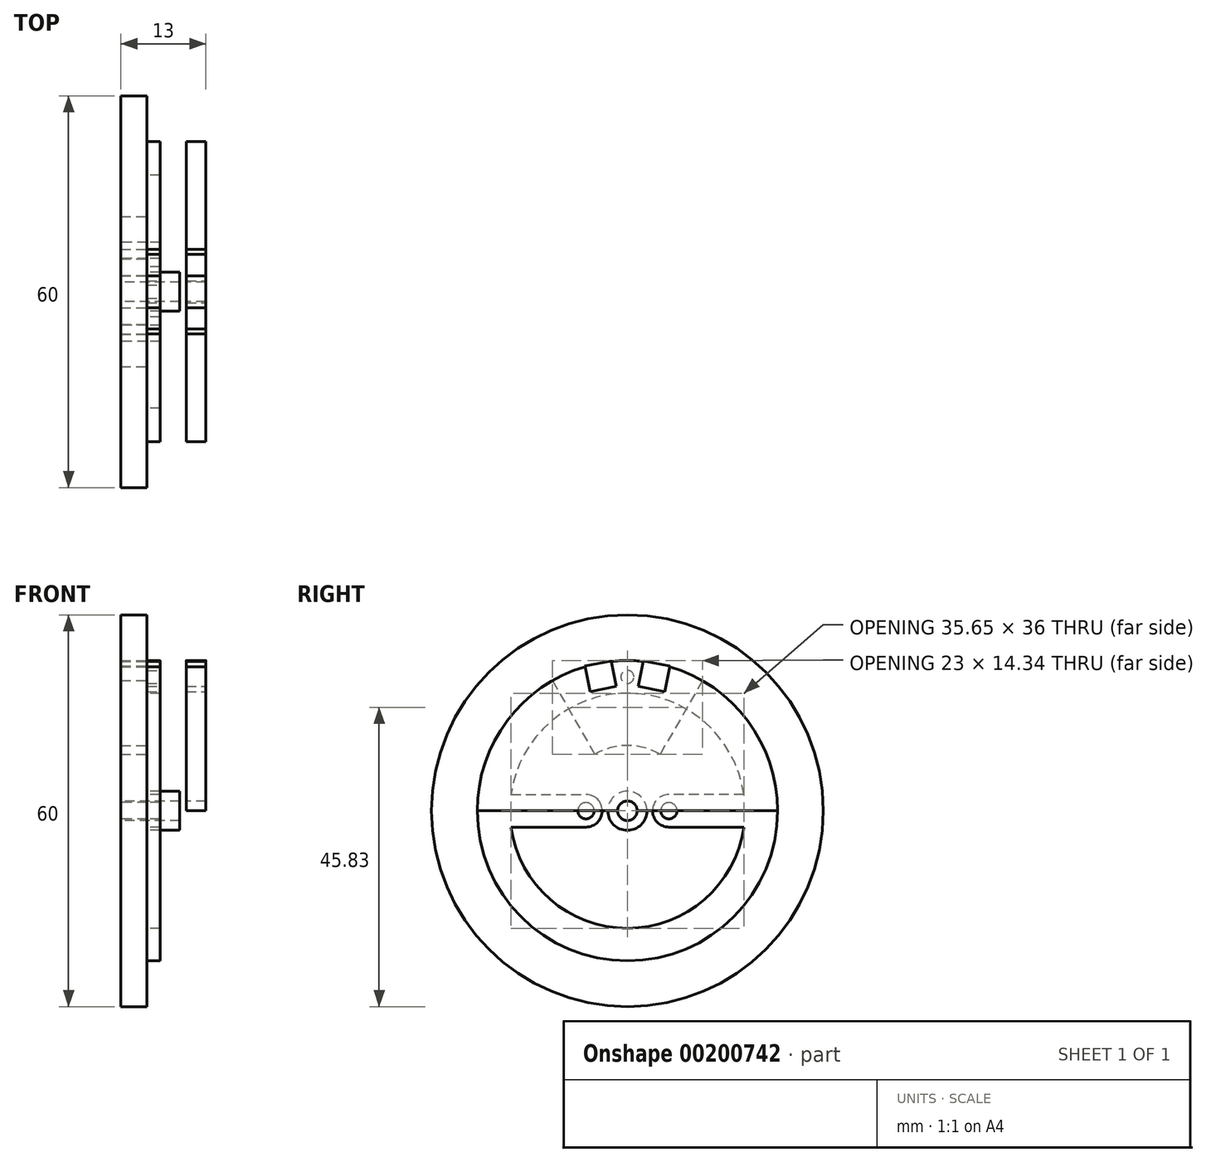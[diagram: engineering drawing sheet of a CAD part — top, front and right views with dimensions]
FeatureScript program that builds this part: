
annotation { "Feature Type Name" : "Feature", "Feature Type Description" : "" }
export const myFeature = defineFeature(function(context is Context, id is Id, definition is map)
    precondition{}
    {
        {
            var Q0;
            Q0=qCreatedBy(makeId("Right.planeOp"),FACE);
            var sketch = newSketch(context, id + "F0", { "sketchPlane" : qUnion([Q0])});
            skCircle(sketch, "E0", {"center": v(0, 0) * mm, "radius": 30 * mm});
            skSolve(sketch);
        }
        {
            var Q0;
            Q0 = qSketchRegion(id + "F0", true);
            extrude(context, id + "F1", {"entities" : qUnion([Q0]), "depth" : 4 * mm, "offsetDistance" : 25 * mm});
        }
        {
            var Q0;
            Q0=makeQuery(id+"F1.opExtrude","CAP_FACE",FACE,{"disambiguationData":[OSD([sQuery(id+"F0.wireOp",EDGE,"E0")])],"isStart":false});
            var sketch = newSketch(context, id + "F2", { "sketchPlane" : qUnion([Q0])});
            skCircle(sketch, "E1", {"center": v(0, 0) * mm, "radius": 3 * mm});
            skSolve(sketch);
        }
        {
            var Q0;
            Q0 = qSketchRegion(id + "F2", true);
            extrude(context, id + "F3", {"entities" : qUnion([Q0]), "operationType" : NewBodyOperationType.ADD, "depth" : 5 * mm, "offsetDistance" : 25 * mm});
        }
        {
            var Q0;
            Q0=makeQuery(id+"F1.opExtrude","CAP_FACE",FACE,{"disambiguationData":[OSD([sQuery(id+"F0.wireOp",EDGE,"E0")])],"isStart":true});
            var sketch = newSketch(context, id + "F4", { "sketchPlane" : qUnion([Q0])});
            skCircle(sketch, "E2", {"center": v(-6.35, 0) * mm, "radius": 1.25 * mm});
            skCircle(sketch, "E3.MirrorC", {"center": v(6.35, 0) * mm, "radius": 1.25 * mm});
            skCircle(sketch, "E4", {"center": v(0, 0) * mm, "radius": 1.5 * mm});
            skSolve(sketch);
        }
        {
            var Q0;
            Q0 = qSketchRegion(id + "F4", true);
            extrude(context, id + "F5", {"entities" : qUnion([Q0]), "operationType" : NewBodyOperationType.REMOVE, "endBound" : BoundingType.THROUGH_ALL, "oppositeDirection" : true, "depth" : 25 * mm, "offsetDistance" : 25 * mm});
        }
        {
            var Q0;
            Q0=makeQuery(id+"F1.opExtrude","CAP_FACE",FACE,{"disambiguationData":[OSD([sQuery(id+"F0.wireOp",EDGE,"E0")])],"isStart":false});
            var sketch = newSketch(context, id + "F6", { "sketchPlane" : qUnion([Q0])});
            skArc(sketch, "E5", {"start": v(11.5, 19.92) * mm, "mid": v(0, 23) * mm, "end": v(-11.5, 19.92) * mm});
            skArc(sketch, "E6", {"start": v(5, 8.66) * mm, "mid": v(0, 10) * mm, "end": v(-5, 8.66) * mm});
            skLineSegment(sketch, "E7", {"start": v(-11.5, 19.92) * mm, "end": v(-5, 8.66) * mm});
            skLineSegment(sketch, "E8", {"start": v(11.5, 19.92) * mm, "end": v(5, 8.66) * mm});
            skSolve(sketch);
        }
        {
            var Q0;
            Q0 = qSketchRegion(id + "F6", true);
            extrude(context, id + "F7", {"entities" : qUnion([Q0]), "operationType" : NewBodyOperationType.REMOVE, "endBound" : BoundingType.THROUGH_ALL, "oppositeDirection" : true, "depth" : 25 * mm, "offsetDistance" : 25 * mm});
        }
        {
            var Q0;
            Q0=makeQuery(id+"F1.opExtrude","CAP_FACE",FACE,{"disambiguationData":[OSD([sQuery(id+"F0.wireOp",EDGE,"E0")])],"isStart":false});
            var sketch = newSketch(context, id + "F8", { "sketchPlane" : qUnion([Q0])});
            skCircle(sketch, "E9", {"center": v(0, 0) * mm, "radius": 23 * mm});
            skArc(sketch, "E10", {"start": v(-17.83, -2.5) * mm, "mid": v(0, -18) * mm, "end": v(17.83, -2.5) * mm});
            skLineSegment(sketch, "E11.bottom", {"start": v(-17.83, 2.5) * mm, "end": v(-6.35, 2.5) * mm});
            skLineSegment(sketch, "E11.top", {"start": v(-17.83, -2.5) * mm, "end": v(-6.35, -2.5) * mm});
            skArc(sketch, "E12", {"start": v(-6.35, -2.5) * mm, "mid": v(-3.85, 0) * mm, "end": v(-6.35, 2.5) * mm});
            skLineSegment(sketch, "E13.MirrorCS", {"start": v(17.83, 2.5) * mm, "end": v(6.35, 2.5) * mm});
            skArc(sketch, "E14.MirrorCS", {"start": v(6.35, -2.5) * mm, "mid": v(3.85, 0) * mm, "end": v(6.35, 2.5) * mm});
            skLineSegment(sketch, "E15.MirrorCS", {"start": v(17.83, -2.5) * mm, "end": v(6.35, -2.5) * mm});
            skPoint(sketch, "E11.left.end.orphan", {"position": v(-22.86, -2.5) * mm});
            skPoint(sketch, "E11.left.start.orphan", {"position": v(-22.86, 2.5) * mm});
            skPoint(sketch, "E16.orphan", {"position": v(22.86, 2.5) * mm});
            skArc(sketch, "E17.trimOffspring", {"start": v(17.83, 2.5) * mm, "mid": v(0, 18) * mm, "end": v(-17.83, 2.5) * mm});
            skPoint(sketch, "E18.orphan", {"position": v(22.86, -2.5) * mm});
            skCircle(sketch, "E19.0", {"center": v(-6.35, 0) * mm, "radius": 1.25 * mm});
            skCircle(sketch, "E20.0", {"center": v(6.35, 0) * mm, "radius": 1.25 * mm});
            skSolve(sketch);
        }
        {
            var Q0;
            Q0 = qSketchRegion(id + "F8", true);
            extrude(context, id + "F9", {"entities" : qUnion([Q0]), "depth" : 2 * mm, "offsetDistance" : 25 * mm});
        }
        {
            var Q0;
            Q0=makeQuery(id+"F9.opExtrude","CAP_FACE",FACE,{"disambiguationData":[OSD([sQuery(id+"F8.wireOp",EDGE,"E9"),sQuery(id+"F8.wireOp",EDGE,"E10"),sQuery(id+"F8.wireOp",EDGE,"E11.bottom"),sQuery(id+"F8.wireOp",EDGE,"E11.top"),sQuery(id+"F8.wireOp",EDGE,"E12"),sQuery(id+"F8.wireOp",EDGE,"E13.MirrorCS"),sQuery(id+"F8.wireOp",EDGE,"E14.MirrorCS"),sQuery(id+"F8.wireOp",EDGE,"E15.MirrorCS"),sQuery(id+"F8.wireOp",EDGE,"E17.trimOffspring")])],"isStart":false});
            var sketch = newSketch(context, id + "F10", { "sketchPlane" : qUnion([Q0])});
            skCircle(sketch, "E21", {"center": v(0, 20.5) * mm, "radius": 1 * mm});
            skSolve(sketch);
        }
        {
            var Q0;
            Q0 = qSketchRegion(id + "F10", true);
            extrude(context, id + "F11", {"entities" : qUnion([Q0]), "operationType" : NewBodyOperationType.REMOVE, "endBound" : BoundingType.THROUGH_ALL, "oppositeDirection" : true, "depth" : 25 * mm, "offsetDistance" : 25 * mm});
        }
        {
            var Q0;
            Q0=qCreatedBy(makeId("Right.planeOp"),FACE);
            cPlane(context, id + "F12", {"entities" : qUnion([Q0]), "cplaneType" : CPlaneType.OFFSET, "offset" : 10 * mm, "width" : 150 * mm, "height" : 150 * mm});
        }
        {
            var Q0;
            Q0=qCreatedBy(id+"F12.planeOp",FACE);
            var sketch = newSketch(context, id + "F13", { "sketchPlane" : qUnion([Q0])});
            skArc(sketch, "E22", {"start": v(23, 0) * mm, "mid": v(0, 23) * mm, "end": v(-23, 0) * mm});
            skLineSegment(sketch, "E23", {"start": v(-23, 0) * mm, "end": v(-1.5, 0) * mm});
            skArc(sketch, "E24.0", {"start": v(1.5, 0) * mm, "mid": v(0, 1.5) * mm, "end": v(-1.5, 0) * mm});
            skLineSegment(sketch, "E25.trimOffspring", {"start": v(1.5, 0) * mm, "end": v(23, 0) * mm});
            skSolve(sketch);
        }
        {
            var Q0;
            Q0 = qSketchRegion(id + "F13", true);
            extrude(context, id + "F14", {"entities" : qUnion([Q0]), "depth" : 3 * mm, "offsetDistance" : 25 * mm});
        }
        {
            var Q0;
            Q0=makeQuery(id+"F14.opExtrude","CAP_FACE",FACE,{"disambiguationData":[OSD([sQuery(id+"F13.wireOp",EDGE,"E22"),sQuery(id+"F13.wireOp",EDGE,"E23")])],"isStart":false});
            var sketch = newSketch(context, id + "F15", { "sketchPlane" : qUnion([Q0])});
            skLineSegment(sketch, "E26", {"start": v(-6.5, 22.16) * mm, "end": v(-5.73, 18.23) * mm});
            skLineSegment(sketch, "E27", {"start": v(-5.73, 18.23) * mm, "end": v(-1.69, 19.04) * mm});
            skLineSegment(sketch, "E28", {"start": v(-1.69, 19.04) * mm, "end": v(-2.47, 22.96) * mm});
            skLineSegment(sketch, "E29", {"start": v(-2.47, 22.96) * mm, "end": v(-6.5, 22.16) * mm});
            skLineSegment(sketch, "E30", {"start": v(-6.31, 21.18) * mm, "end": v(-2.27, 21.98) * mm, "construction": true});
            skLineSegment(sketch, "E31", {"start": v(-6.31, 21.18) * mm, "end": v(-1.69, 19.04) * mm, "construction": true});
            skPoint(sketch, "E32", {"position": v(-4, 20.1) * mm});
            skLineSegment(sketch, "E33", {"start": v(-4, 20.1) * mm, "end": v(-3.7, 18.63) * mm, "construction": true});
            skLineSegment(sketch, "E34.MirrorCS", {"start": v(1.69, 19.04) * mm, "end": v(2.47, 22.96) * mm});
            skLineSegment(sketch, "E35.MirrorCS", {"start": v(5.73, 18.23) * mm, "end": v(1.69, 19.04) * mm});
            skLineSegment(sketch, "E36.MirrorCS", {"start": v(6.31, 21.18) * mm, "end": v(2.27, 21.98) * mm, "construction": true});
            skLineSegment(sketch, "E37.MirrorCS", {"start": v(4, 20.1) * mm, "end": v(3.7, 18.63) * mm, "construction": true});
            skLineSegment(sketch, "E38.MirrorCS", {"start": v(6.31, 21.18) * mm, "end": v(1.69, 19.04) * mm, "construction": true});
            skPoint(sketch, "E39.MirrorP", {"position": v(4, 20.1) * mm});
            skLineSegment(sketch, "E40.MirrorCS", {"start": v(6.5, 22.16) * mm, "end": v(5.73, 18.23) * mm});
            skLineSegment(sketch, "E41.MirrorCS", {"start": v(2.47, 22.96) * mm, "end": v(6.5, 22.16) * mm});
            skSolve(sketch);
        }
        {
            var Q0;
            Q0 = qSketchRegion(id + "F15", true);
            extrude(context, id + "F16", {"entities" : qUnion([Q0]), "operationType" : NewBodyOperationType.REMOVE, "endBound" : BoundingType.THROUGH_ALL, "oppositeDirection" : true, "depth" : 25 * mm, "offsetDistance" : 25 * mm});
        }
    });
